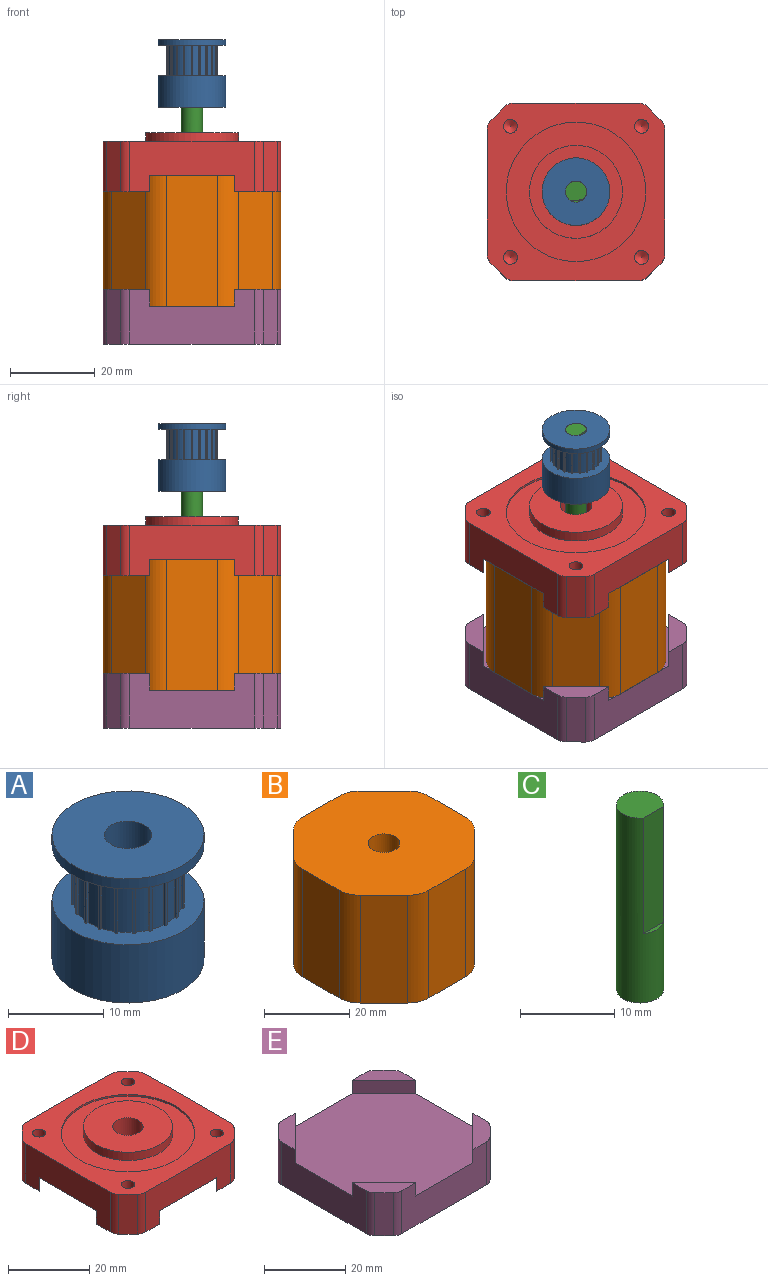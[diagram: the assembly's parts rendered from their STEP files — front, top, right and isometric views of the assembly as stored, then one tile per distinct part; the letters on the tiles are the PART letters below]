
ASSEMBLY  parts=5 mates=4
PART A: 87 faces, bbox 16x16x16 mm
  f0: plane 16x16mm, normal (0,0,1), area 95.7mm2, adj f2,f4,f5,f6,f7,f8,f9,f10
  f1: cylinder r=2.5mm len=16mm, axis (0,0,-1), area 251.3mm2, adj f3,f86
  f2: cylinder r=8mm len=16mm, axis (0,0,-1), area 377mm2, adj f0,f3
  f3: plane 16x16mm, normal (0,0,-1), area 181.4mm2, adj f1,f2
  f4: plane 7.2x0.2mm, normal (-0.6,0.8,0), area 1.8mm2, adj f0,f5,f83,f84
  f5: cylinder r=6mm len=7.2mm, axis (0,0,-1), area 2mm2, adj f0,f4,f6,f84
  f6: plane 7.2x0.21mm, normal (0.53,-0.85,0), area 1.8mm2, adj f0,f5,f7,f84
  f7: cylinder r=5.75mm len=7.2mm, axis (0,0,-1), area 10.8mm2, adj f0,f6,f8,f84
  f8: plane 7.2x0.21mm, normal (-0.82,0.57,0), area 1.8mm2, adj f0,f7,f9,f84
  f9: cylinder r=6mm len=7.2mm, axis (0,0,-1), area 2mm2, adj f0,f8,f10,f84
  f10: plane 7.2x0.19mm, normal (0.77,-0.64,0), area 1.8mm2, adj f0,f9,f11,f84
  f11: cylinder r=5.75mm len=7.2mm, axis (0,0,-1), area 10.8mm2, adj f0,f10,f12,f84
  f12: plane 7.2x0.24mm, normal (-0.96,0.29,0), area 1.8mm2, adj f0,f11,f13,f84
  f13: cylinder r=6mm len=7.2mm, axis (0,0,-1), area 2mm2, adj f0,f12,f14,f84
  f14: plane 7.2x0.23mm, normal (0.93,-0.37,0), area 1.8mm2, adj f0,f13,f15,f84
  f15: cylinder r=5.75mm len=7.2mm, axis (0,0,-1), area 10.8mm2, adj f0,f14,f16,f84
  f16: plane 7.2x0.25mm, normal (-1,-0.02,0), area 1.8mm2, adj f0,f15,f17,f84
  f17: cylinder r=6mm len=7.2mm, axis (0,0,-1), area 2mm2, adj f0,f16,f18,f84
  f18: plane 7.2x0.25mm, normal (1,-0.07,0), area 1.8mm2, adj f0,f17,f19,f84
  f19: cylinder r=5.75mm len=7.2mm, axis (0,0,-1), area 10.8mm2, adj f0,f18,f20,f84
  f20: plane 7.2x0.24mm, normal (-0.94,-0.33,0), area 1.8mm2, adj f0,f19,f21,f84
  f21: cylinder r=6mm len=7.2mm, axis (0,0,-1), area 2mm2, adj f0,f20,f22,f84
  f22: plane 7.2x0.24mm, normal (0.97,0.25,0), area 1.8mm2, adj f0,f21,f23,f84
  f23: cylinder r=5.75mm len=7.2mm, axis (0,0,-1), area 10.8mm2, adj f0,f22,f24,f84
  f24: plane 7.2x0.2mm, normal (-0.8,-0.6,0), area 1.8mm2, adj f0,f23,f25,f84
  f25: cylinder r=6mm len=7.2mm, axis (0,0,-1), area 2mm2, adj f0,f24,f26,f84
  f26: plane 7.2x0.21mm, normal (0.85,0.53,0), area 1.8mm2, adj f0,f25,f27,f84
  f27: cylinder r=5.75mm len=7.2mm, axis (0,0,-1), area 10.8mm2, adj f0,f26,f28,f84
  f28: plane 7.2x0.21mm, normal (-0.57,-0.82,0), area 1.8mm2, adj f0,f27,f29,f84
  f29: cylinder r=6mm len=7.2mm, axis (0,0,-1), area 2mm2, adj f0,f28,f30,f84
  f30: plane 7.2x0.19mm, normal (0.64,0.77,0), area 1.8mm2, adj f0,f29,f31,f84
  f31: cylinder r=5.75mm len=7.2mm, axis (0,0,-1), area 10.8mm2, adj f0,f30,f32,f84
  f32: plane 7.2x0.24mm, normal (-0.29,-0.96,0), area 1.8mm2, adj f0,f31,f33,f84
  f33: cylinder r=6mm len=7.2mm, axis (0,0,-1), area 2mm2, adj f0,f32,f34,f84
  f34: plane 7.2x0.23mm, normal (0.37,0.93,0), area 1.8mm2, adj f0,f33,f35,f84
  f35: cylinder r=5.75mm len=7.2mm, axis (0,0,-1), area 10.8mm2, adj f0,f34,f36,f84
  f36: plane 7.2x0.25mm, normal (0.02,-1,0), area 1.8mm2, adj f0,f35,f37,f84
  f37: cylinder r=6mm len=7.2mm, axis (0,0,-1), area 2mm2, adj f0,f36,f38,f84
  f38: plane 7.2x0.25mm, normal (0.07,1,0), area 1.8mm2, adj f0,f37,f39,f84
  f39: cylinder r=5.75mm len=7.2mm, axis (0,0,-1), area 10.8mm2, adj f0,f38,f40,f84
  f40: plane 7.2x0.24mm, normal (0.33,-0.94,0), area 1.8mm2, adj f0,f39,f41,f84
  f41: cylinder r=6mm len=7.2mm, axis (0,0,-1), area 2mm2, adj f0,f40,f42,f84
  f42: plane 7.2x0.24mm, normal (-0.25,0.97,0), area 1.8mm2, adj f0,f41,f43,f84
  f43: cylinder r=5.75mm len=7.2mm, axis (0,0,-1), area 10.8mm2, adj f0,f42,f44,f84
  f44: plane 7.2x0.2mm, normal (0.6,-0.8,0), area 1.8mm2, adj f0,f43,f45,f84
  f45: cylinder r=6mm len=7.2mm, axis (0,0,-1), area 2mm2, adj f0,f44,f46,f84
  f46: plane 7.2x0.21mm, normal (-0.53,0.85,0), area 1.8mm2, adj f0,f45,f47,f84
  f47: cylinder r=5.75mm len=7.2mm, axis (0,0,-1), area 10.8mm2, adj f0,f46,f48,f84
  f48: plane 7.2x0.21mm, normal (0.82,-0.57,0), area 1.8mm2, adj f0,f47,f49,f84
  f49: cylinder r=6mm len=7.2mm, axis (0,0,-1), area 2mm2, adj f0,f48,f50,f84
  f50: plane 7.2x0.19mm, normal (-0.77,0.64,0), area 1.8mm2, adj f0,f49,f51,f84
  f51: cylinder r=5.75mm len=7.2mm, axis (0,0,-1), area 10.8mm2, adj f0,f50,f52,f84
  f52: plane 7.2x0.24mm, normal (0.96,-0.29,0), area 1.8mm2, adj f0,f51,f53,f84
  f53: cylinder r=6mm len=7.2mm, axis (0,0,-1), area 2mm2, adj f0,f52,f54,f84
  f54: plane 7.2x0.23mm, normal (-0.93,0.37,0), area 1.8mm2, adj f0,f53,f55,f84
  f55: cylinder r=5.75mm len=7.2mm, axis (0,0,-1), area 10.8mm2, adj f0,f54,f56,f84
  f56: plane 7.2x0.25mm, normal (1,0.02,0), area 1.8mm2, adj f0,f55,f57,f84
  f57: cylinder r=6mm len=7.2mm, axis (0,0,-1), area 2mm2, adj f0,f56,f58,f84
  f58: plane 7.2x0.25mm, normal (-1,0.07,0), area 1.8mm2, adj f0,f57,f59,f84
  f59: cylinder r=5.75mm len=7.2mm, axis (0,0,-1), area 10.8mm2, adj f0,f58,f60,f84
  f60: plane 7.2x0.24mm, normal (0.94,0.33,0), area 1.8mm2, adj f0,f59,f61,f84
  f61: cylinder r=6mm len=7.2mm, axis (0,0,-1), area 2mm2, adj f0,f60,f62,f84
  f62: plane 7.2x0.24mm, normal (-0.97,-0.25,0), area 1.8mm2, adj f0,f61,f63,f84
  f63: cylinder r=5.75mm len=7.2mm, axis (0,0,-1), area 10.8mm2, adj f0,f62,f64,f84
  f64: plane 7.2x0.2mm, normal (0.8,0.6,0), area 1.8mm2, adj f0,f63,f65,f84
  f65: cylinder r=6mm len=7.2mm, axis (0,0,-1), area 2mm2, adj f0,f64,f66,f84
  f66: plane 7.2x0.21mm, normal (-0.85,-0.53,0), area 1.8mm2, adj f0,f65,f67,f84
  f67: cylinder r=5.75mm len=7.2mm, axis (0,0,-1), area 10.8mm2, adj f0,f66,f68,f84
  f68: plane 7.2x0.21mm, normal (0.57,0.82,0), area 1.8mm2, adj f0,f67,f69,f84
  f69: cylinder r=6mm len=7.2mm, axis (0,0,-1), area 2mm2, adj f0,f68,f70,f84
  f70: plane 7.2x0.19mm, normal (-0.64,-0.77,0), area 1.8mm2, adj f0,f69,f71,f84
  f71: cylinder r=5.75mm len=7.2mm, axis (0,0,-1), area 10.8mm2, adj f0,f70,f72,f84
  f72: plane 7.2x0.24mm, normal (0.29,0.96,0), area 1.8mm2, adj f0,f71,f73,f84
  f73: cylinder r=6mm len=7.2mm, axis (0,0,-1), area 2mm2, adj f0,f72,f74,f84
  f74: plane 7.2x0.23mm, normal (-0.37,-0.93,0), area 1.8mm2, adj f0,f73,f75,f84
  f75: cylinder r=5.75mm len=7.2mm, axis (0,0,-1), area 10.8mm2, adj f0,f74,f76,f84
  f76: plane 7.2x0.25mm, normal (-0.02,1,0), area 1.8mm2, adj f0,f75,f77,f84
  f77: cylinder r=6mm len=7.2mm, axis (0,0,-1), area 2mm2, adj f0,f76,f78,f84
  f78: plane 7.2x0.25mm, normal (-0.07,-1,0), area 1.8mm2, adj f0,f77,f79,f84
  f79: cylinder r=5.75mm len=7.2mm, axis (0,0,-1), area 10.8mm2, adj f0,f78,f80,f84
  f80: plane 7.2x0.24mm, normal (-0.33,0.94,0), area 1.8mm2, adj f0,f79,f81,f84
  f81: cylinder r=6mm len=7.2mm, axis (0,0,-1), area 2mm2, adj f0,f80,f82,f84
  f82: plane 7.2x0.24mm, normal (0.25,-0.97,0), area 1.8mm2, adj f0,f81,f83,f84
  f83: cylinder r=5.75mm len=7.2mm, axis (0,0,-1), area 10.8mm2, adj f0,f4,f82,f84
  f84: plane 16x16mm, normal (0,0,-1), area 95.7mm2, adj f4,f5,f6,f7,f8,f9,f10,f11
  f85: cylinder r=8mm len=16mm, axis (0,0,-1), area 65.3mm2, adj f84,f86
  f86: plane 16x16mm, normal (0,0,1), area 181.4mm2, adj f1,f85
PART B: 19 faces, bbox 42x42x31 mm
  f0: plane 31x12.2mm, normal (0,-1,0), area 378.2mm2, adj f5,f6,f17,f18
  f1: plane 31x12.2mm, normal (-1,0,0), area 378.2mm2, adj f5,f6,f13,f14
  f2: plane 31x12.2mm, normal (0,1,0), area 378.2mm2, adj f5,f6,f11,f12
  f3: plane 31x12.2mm, normal (1,0,0), area 378.2mm2, adj f5,f6,f15,f16
  f4: cylinder r=3.75mm len=31mm, axis (0,0,1), area 730.4mm2, adj f5,f6
  f5: plane 42x42mm, normal (0,0,-1), area 1423.4mm2, adj f0,f1,f2,f3,f4,f7,f8,f9
  f6: plane 42x42mm, normal (0,0,1), area 1423.4mm2, adj f0,f1,f2,f3,f4,f7,f8,f9
  f7: plane 31x7.9mm, normal (0.71,-0.71,0), area 346.3mm2, adj f5,f6,f15,f17
  f8: plane 31x7.9mm, normal (-0.71,-0.71,0), area 346.3mm2, adj f5,f6,f13,f18
  f9: plane 31x7.9mm, normal (0.71,0.71,0), area 346.3mm2, adj f5,f6,f11,f16
  f10: plane 31x7.9mm, normal (-0.71,0.71,0), area 346.3mm2, adj f5,f6,f12,f14
  f11: cylinder r=7mm len=31mm, axis (0,0,1), area 170.4mm2, adj f2,f5,f6,f9
  f12: cylinder r=7mm len=31mm, axis (0,0,1), area 170.4mm2, adj f2,f5,f6,f10
  f13: cylinder r=7mm len=31mm, axis (0,0,1), area 170.4mm2, adj f1,f5,f6,f8
  f14: cylinder r=7mm len=31mm, axis (0,0,1), area 170.4mm2, adj f1,f5,f6,f10
  f15: cylinder r=7mm len=31mm, axis (0,0,-1), area 170.4mm2, adj f3,f5,f6,f7
  f16: cylinder r=7mm len=31mm, axis (0,0,-1), area 170.4mm2, adj f3,f5,f6,f9
  f17: cylinder r=7mm len=31mm, axis (0,0,-1), area 170.4mm2, adj f0,f5,f6,f7
  f18: cylinder r=7mm len=31mm, axis (0,0,-1), area 170.4mm2, adj f0,f5,f6,f8
PART C: 5 faces, bbox 5x5x24 mm
  f0: plane 5x4.5mm, normal (0,0,1), area 18.6mm2, adj f1,f3
  f1: cylinder r=2.5mm len=24mm, axis (0,0,-1), area 328.7mm2, adj f0,f2,f3,f4
  f2: plane 5x5mm, normal (0,0,-1), area 19.6mm2, adj f1
  f3: plane 15x3mm, normal (0,-1,0), area 45mm2, adj f0,f1,f4
  f4: plane 3x0.5mm, normal (0,0,1), area 1mm2, adj f1,f3
PART D: 39 faces, bbox 42x42x14 mm
  f0: plane 29.51x12mm, normal (1,0,0), area 274.2mm2, adj f5,f6,f23,f24,f29,f30,f31,f32
  f1: plane 29.51x12mm, normal (0,1,0), area 274.2mm2, adj f5,f6,f27,f28,f29,f30,f37,f38
  f2: plane 29.51x12mm, normal (-1,0,0), area 274.2mm2, adj f5,f6,f25,f26,f27,f28,f35,f36
  f3: plane 29.51x12mm, normal (0,-1,0), area 274.2mm2, adj f5,f6,f23,f24,f25,f26,f33,f34
  f4: cylinder r=3.75mm len=10mm, axis (0,0,1), area 235.6mm2, adj f5,f10
  f5: plane 42x42mm, normal (0,0,-1), area 1477.8mm2, adj f0,f1,f2,f3,f4,f23,f25,f27
  f6: plane 42x42mm, normal (0,0,1), area 822.9mm2, adj f0,f1,f2,f3,f8,f11,f12,f13
  f7: cylinder r=11mm len=22mm, axis (0,0,1), area 172.8mm2, adj f9,f10
  f8: cylinder r=16.5mm len=33mm, axis (0,0,1), area 51.8mm2, adj f6,f9
  f9: plane 33x33mm, normal (0,0,1), area 475.2mm2, adj f7,f8
  f10: plane 22x22mm, normal (0,0,1), area 336mm2, adj f4,f7
  f11: plane 12x3.24mm, normal (-0.71,0.71,0), area 55mm2, adj f6,f28,f35,f37
  f12: plane 12x3.24mm, normal (-0.71,-0.71,0), area 55mm2, adj f6,f26,f33,f36
  f13: plane 12x3.24mm, normal (0.71,0.71,0), area 55mm2, adj f6,f30,f31,f38
  f14: plane 12x3.24mm, normal (0.71,-0.71,0), area 55mm2, adj f6,f24,f32,f34
  f15: cylinder r=1.65mm len=6mm, axis (0,0,1), area 62.2mm2, adj f6,f16
  f16: cone r=0mm half-angle=59deg, axis (0,0,1), area 10mm2, adj f15
  f17: cylinder r=1.65mm len=6mm, axis (0,0,1), area 62.2mm2, adj f6,f18
  f18: cone r=0mm half-angle=59deg, axis (0,0,1), area 10mm2, adj f17
  f19: cylinder r=1.65mm len=6mm, axis (0,0,1), area 62.2mm2, adj f6,f20
  f20: cone r=0mm half-angle=59deg, axis (0,0,1), area 10mm2, adj f19
  f21: cylinder r=1.65mm len=6mm, axis (0,0,1), area 62.2mm2, adj f6,f22
  f22: cone r=0mm half-angle=59deg, axis (0,0,1), area 10mm2, adj f21
  f23: plane 11x11mm, normal (-0.71,0.71,0), area 62.2mm2, adj f0,f3,f5,f24
  f24: plane 11x11mm, normal (0,0,-1), area 47.6mm2, adj f0,f3,f14,f23,f32,f34
  f25: plane 11x11mm, normal (0.71,0.71,0), area 62.2mm2, adj f2,f3,f5,f26
  f26: plane 11x11mm, normal (0,0,-1), area 47.6mm2, adj f2,f3,f12,f25,f33,f36
  f27: plane 11x11mm, normal (0.71,-0.71,0), area 62.2mm2, adj f1,f2,f5,f28
  f28: plane 11x11mm, normal (0,0,-1), area 47.6mm2, adj f1,f2,f11,f27,f35,f37
  f29: plane 11x11mm, normal (-0.71,-0.71,0), area 62.2mm2, adj f0,f1,f5,f30
  f30: plane 11x11mm, normal (0,0,-1), area 47.6mm2, adj f0,f1,f13,f29,f31,f38
  f31: cylinder r=3mm len=12mm, axis (0,0,-1), area 28.3mm2, adj f0,f6,f13,f30
  f32: cylinder r=3mm len=12mm, axis (0,0,-1), area 28.3mm2, adj f0,f6,f14,f24
  f33: cylinder r=3mm len=12mm, axis (0,0,-1), area 28.3mm2, adj f3,f6,f12,f26
  f34: cylinder r=3mm len=12mm, axis (0,0,-1), area 28.3mm2, adj f3,f6,f14,f24
  f35: cylinder r=3mm len=12mm, axis (0,0,1), area 28.3mm2, adj f2,f6,f11,f28
  f36: cylinder r=3mm len=12mm, axis (0,0,1), area 28.3mm2, adj f2,f6,f12,f26
  f37: cylinder r=3mm len=12mm, axis (0,0,1), area 28.3mm2, adj f1,f6,f11,f28
  f38: cylinder r=3mm len=12mm, axis (0,0,1), area 28.3mm2, adj f1,f6,f13,f30
PART E: 26 faces, bbox 42x42x13 mm
  f0: plane 29.51x13mm, normal (0,1,0), area 303.7mm2, adj f4,f5,f10,f11,f16,f17,f22,f23
  f1: plane 29.51x13mm, normal (1,0,0), area 303.7mm2, adj f4,f5,f14,f15,f16,f17,f24,f25
  f2: plane 29.51x13mm, normal (0,-1,0), area 303.7mm2, adj f4,f5,f12,f13,f14,f15,f20,f21
  f3: plane 29.51x13mm, normal (-1,0,0), area 303.7mm2, adj f4,f5,f10,f11,f12,f13,f18,f19
  f4: plane 42x42mm, normal (0,0,-1), area 1712.5mm2, adj f0,f1,f2,f3,f6,f7,f8,f9
  f5: plane 42x42mm, normal (0,0,1), area 1522mm2, adj f0,f1,f2,f3,f10,f12,f14,f16
  f6: plane 13x3.24mm, normal (0.71,0.71,0), area 59.6mm2, adj f4,f17,f22,f24
  f7: plane 13x3.24mm, normal (0.71,-0.71,0), area 59.6mm2, adj f4,f15,f20,f25
  f8: plane 13x3.24mm, normal (-0.71,0.71,0), area 59.6mm2, adj f4,f11,f18,f23
  f9: plane 13x3.24mm, normal (-0.71,-0.71,0), area 59.6mm2, adj f4,f13,f19,f21
  f10: plane 11x11mm, normal (0.71,-0.71,0), area 62.2mm2, adj f0,f3,f5,f11
  f11: plane 11x11mm, normal (0,0,1), area 47.6mm2, adj f0,f3,f8,f10,f18,f23
  f12: plane 11x11mm, normal (0.71,0.71,0), area 62.2mm2, adj f2,f3,f5,f13
  f13: plane 11x11mm, normal (0,0,1), area 47.6mm2, adj f2,f3,f9,f12,f19,f21
  f14: plane 11x11mm, normal (-0.71,0.71,0), area 62.2mm2, adj f1,f2,f5,f15
  f15: plane 11x11mm, normal (0,0,1), area 47.6mm2, adj f1,f2,f7,f14,f20,f25
  f16: plane 11x11mm, normal (-0.71,-0.71,0), area 62.2mm2, adj f0,f1,f5,f17
  f17: plane 11x11mm, normal (0,0,1), area 47.6mm2, adj f0,f1,f6,f16,f22,f24
  f18: cylinder r=3mm len=13mm, axis (0,0,-1), area 30.6mm2, adj f3,f4,f8,f11
  f19: cylinder r=3mm len=13mm, axis (0,0,-1), area 30.6mm2, adj f3,f4,f9,f13
  f20: cylinder r=3mm len=13mm, axis (0,0,1), area 30.6mm2, adj f2,f4,f7,f15
  f21: cylinder r=3mm len=13mm, axis (0,0,1), area 30.6mm2, adj f2,f4,f9,f13
  f22: cylinder r=3mm len=13mm, axis (0,0,-1), area 30.6mm2, adj f0,f4,f6,f17
  f23: cylinder r=3mm len=13mm, axis (0,0,-1), area 30.6mm2, adj f0,f4,f8,f11
  f24: cylinder r=3mm len=13mm, axis (0,0,1), area 30.6mm2, adj f1,f4,f6,f17
  f25: cylinder r=3mm len=13mm, axis (0,0,1), area 30.6mm2, adj f1,f4,f7,f15
PLACE A rot(axis=(0,0,1),2.5deg) t=(0,0,8)mm
PLACE B at identity
PLACE C rot(axis=(0,0,1),2.5deg) t=(0,0,0)mm
PLACE D at identity
PLACE E at identity fixed
MATE fastened A.f1 <-> C.f1  axis (0,0,-1) through (0,0,24)mm
MATE fastened B.f4 <-> D.f4  axis (0,0,1) through (0,0,-8)mm
MATE revolute D.f4 <-> C.f1  axis (0,0,1) through (0,0,2)mm
MATE fastened E.f5 <-> B.f4  axis (0,0,1) through (0,0,-39)mm
